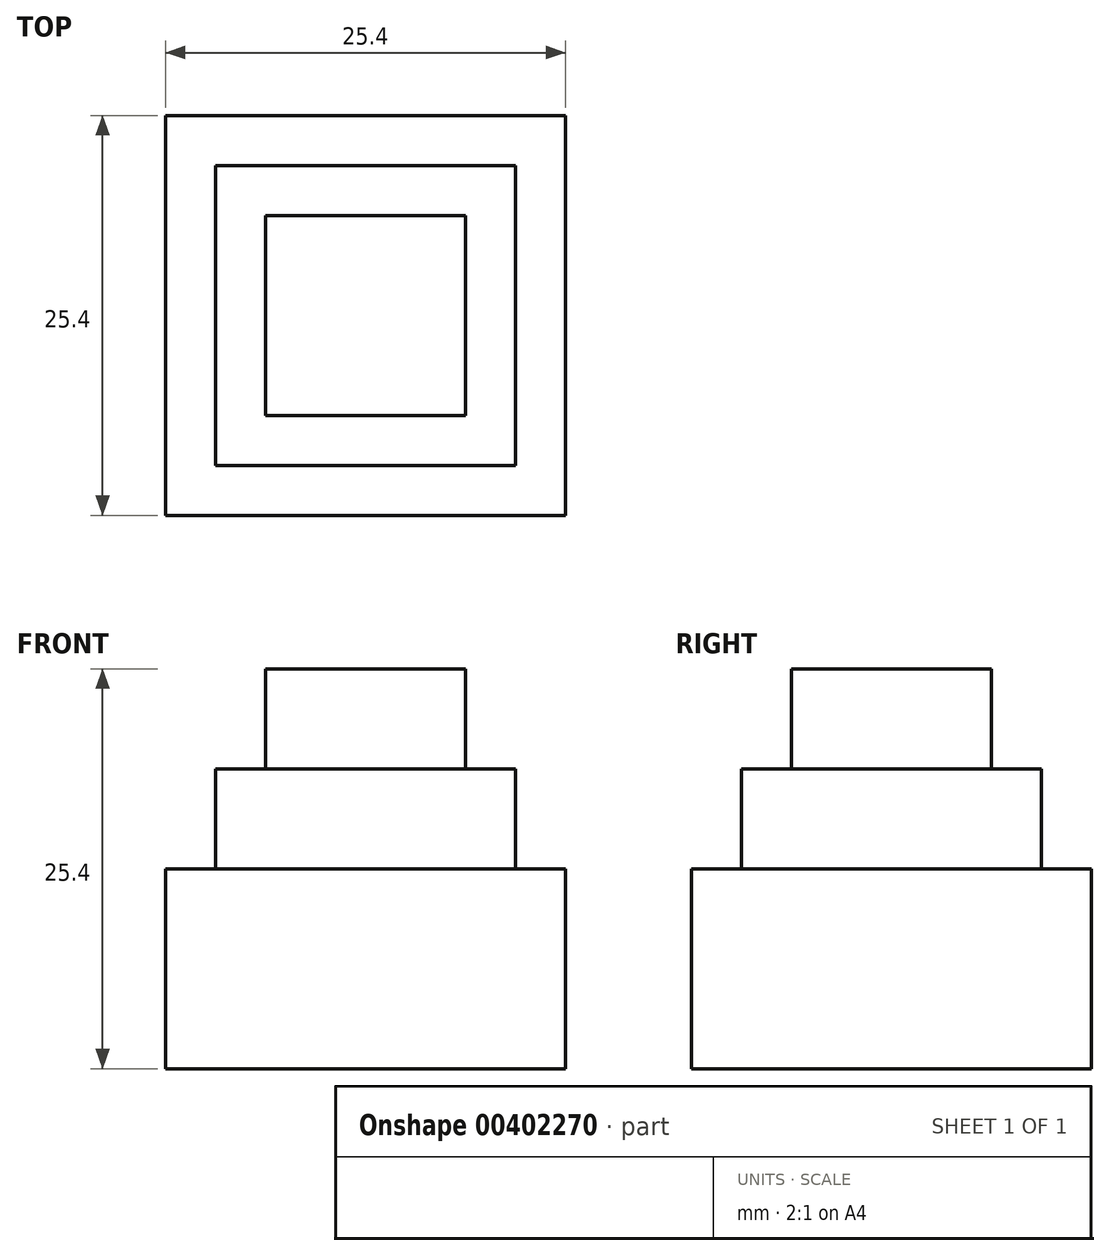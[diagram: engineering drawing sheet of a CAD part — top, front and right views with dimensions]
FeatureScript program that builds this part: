
annotation { "Feature Type Name" : "Feature", "Feature Type Description" : "" }
export const myFeature = defineFeature(function(context is Context, id is Id, definition is map)
    precondition{}
    {
        {
            var Q0;
            Q0=qCreatedBy(makeId("Top.planeOp"),FACE);
            var sketch = newSketch(context, id + "F0", { "sketchPlane" : qUnion([Q0])});
            skLineSegment(sketch, "E0.bottom", {"start": v(12.7, -12.7) * mm, "end": v(-12.7, -12.7) * mm});
            skLineSegment(sketch, "E0.top", {"start": v(12.7, 12.7) * mm, "end": v(-12.7, 12.7) * mm});
            skLineSegment(sketch, "E0.left", {"start": v(12.7, -12.7) * mm, "end": v(12.7, 12.7) * mm});
            skLineSegment(sketch, "E0.right", {"start": v(-12.7, -12.7) * mm, "end": v(-12.7, 12.7) * mm});
            skPoint(sketch, "E0.middle", {"position": v(0, 0) * mm});
            skSolve(sketch);
        }
        {
            var Q0;
            Q0 = qSketchRegion(id + "F0", true);
            extrude(context, id + "F1", {"entities" : qUnion([Q0]), "depth" : 12.7 * mm});
        }
        {
            var Q0;
            Q0=makeQuery(id+"F1.opExtrude","CAP_FACE",FACE,{"disambiguationData":[OSD([sQuery(id+"F0.wireOp",EDGE,"E0.bottom"),sQuery(id+"F0.wireOp",EDGE,"E0.top"),sQuery(id+"F0.wireOp",EDGE,"E0.left"),sQuery(id+"F0.wireOp",EDGE,"E0.right")])],"isStart":false});
            var sketch = newSketch(context, id + "F2", { "sketchPlane" : qUnion([Q0])});
            skLineSegment(sketch, "E1.bottom", {"start": v(9.53, -9.52) * mm, "end": v(-9.53, -9.53) * mm});
            skLineSegment(sketch, "E1.top", {"start": v(9.53, 9.53) * mm, "end": v(-9.53, 9.52) * mm});
            skLineSegment(sketch, "E1.left", {"start": v(9.53, -9.52) * mm, "end": v(9.53, 9.53) * mm});
            skLineSegment(sketch, "E1.right", {"start": v(-9.53, -9.53) * mm, "end": v(-9.53, 9.52) * mm});
            skPoint(sketch, "E1.middle", {"position": v(0, 0) * mm});
            skSolve(sketch);
        }
        {
            var Q0;
            Q0 = qSketchRegion(id + "F2", true);
            extrude(context, id + "F3", {"entities" : qUnion([Q0]), "operationType" : NewBodyOperationType.ADD, "depth" : 6.35 * mm});
        }
        {
            var Q0;
            Q0=makeQuery(id+"F3.opExtrude","CAP_FACE",FACE,{"disambiguationData":[OSD([sQuery(id+"F2.wireOp",EDGE,"E1.bottom"),sQuery(id+"F2.wireOp",EDGE,"E1.top"),sQuery(id+"F2.wireOp",EDGE,"E1.left"),sQuery(id+"F2.wireOp",EDGE,"E1.right")])],"isStart":false});
            var sketch = newSketch(context, id + "F4", { "sketchPlane" : qUnion([Q0])});
            skLineSegment(sketch, "E2.bottom", {"start": v(6.35, 6.35) * mm, "end": v(-6.35, 6.35) * mm});
            skLineSegment(sketch, "E2.top", {"start": v(6.35, -6.35) * mm, "end": v(-6.35, -6.35) * mm});
            skLineSegment(sketch, "E2.left", {"start": v(6.35, 6.35) * mm, "end": v(6.35, -6.35) * mm});
            skLineSegment(sketch, "E2.right", {"start": v(-6.35, 6.35) * mm, "end": v(-6.35, -6.35) * mm});
            skPoint(sketch, "E2.middle", {"position": v(0, 0) * mm});
            skSolve(sketch);
        }
        {
            var Q0;
            Q0 = qSketchRegion(id + "F4", true);
            extrude(context, id + "F5", {"entities" : qUnion([Q0]), "operationType" : NewBodyOperationType.ADD, "depth" : 6.35 * mm});
        }
    });
